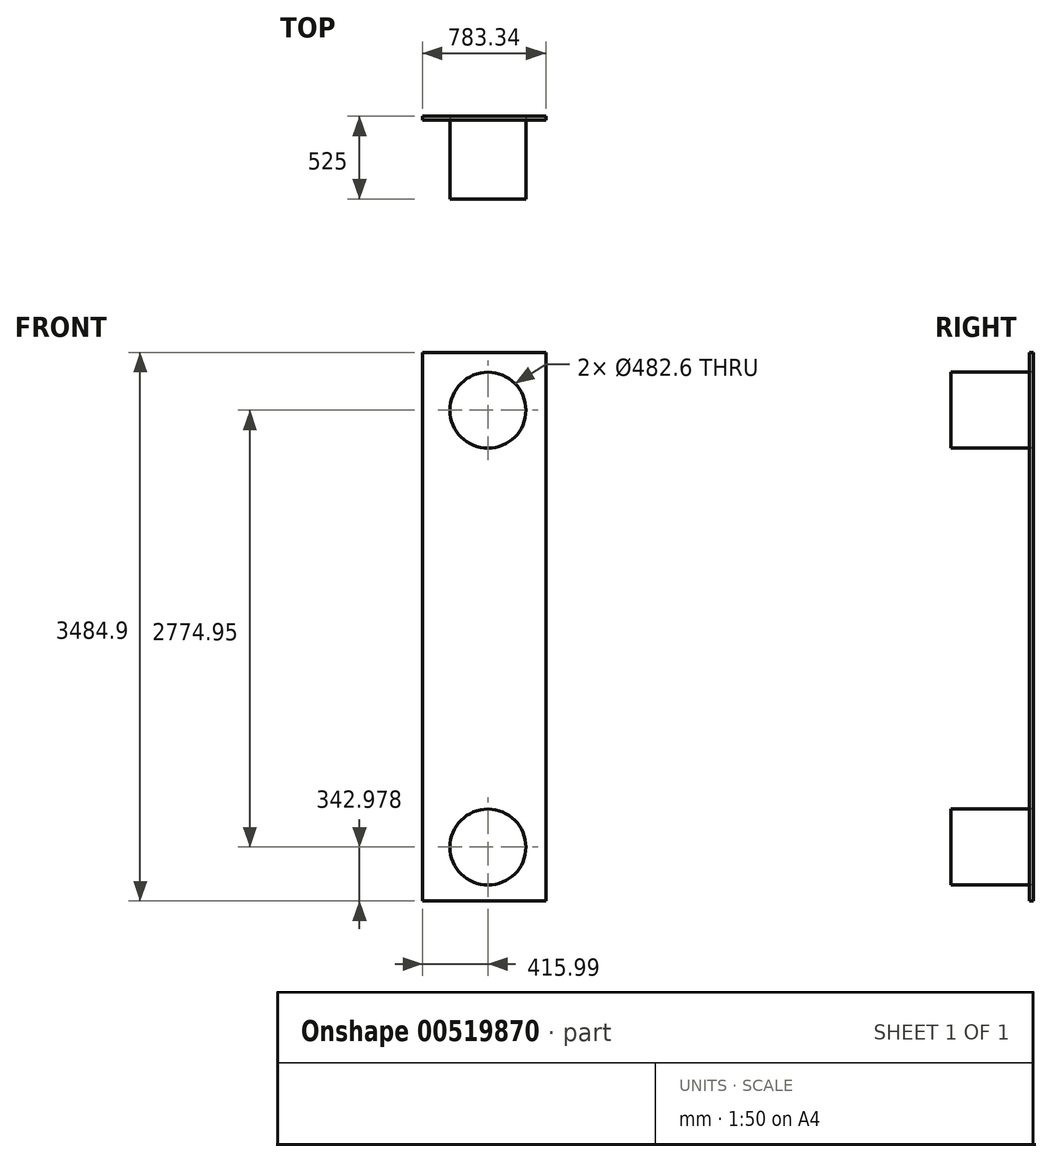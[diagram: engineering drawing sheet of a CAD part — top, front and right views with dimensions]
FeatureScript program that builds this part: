
annotation { "Feature Type Name" : "Feature", "Feature Type Description" : "" }
export const myFeature = defineFeature(function(context is Context, id is Id, definition is map)
    precondition{}
    {
        {
            var Q0;
            Q0=qCreatedBy(makeId("Front.planeOp"),FACE);
            var sketch = newSketch(context, id + "F0", { "sketchPlane" : qUnion([Q0])});
            skCircle(sketch, "E0", {"center": v(0, -900.07) * mm, "radius": 241.3 * mm});
            skCircle(sketch, "E1", {"center": v(0, 1874.88) * mm, "radius": 241.3 * mm});
            skLineSegment(sketch, "E2", {"start": v(0, 1874.88) * mm, "end": v(0, -900.07) * mm, "construction": true});
            skLineSegment(sketch, "E3.bottom", {"start": v(-416, 2241.85) * mm, "end": v(367.35, 2241.85) * mm});
            skLineSegment(sketch, "E3.top", {"start": v(-416, -1243.05) * mm, "end": v(367.35, -1243.05) * mm});
            skLineSegment(sketch, "E3.left", {"start": v(-416, 2241.85) * mm, "end": v(-416, -1243.05) * mm});
            skLineSegment(sketch, "E3.right", {"start": v(367.35, 2241.85) * mm, "end": v(367.35, -1243.05) * mm});
            skSolve(sketch);
        }
        {
            var Q0;
            Q0=makeQuery(id+"F0.imprint","IMPRINT",FACE,{"disambiguationData":[TD([[makeQuery(id+"F0.imprint","IMPRINT",EDGE,{"derivedFrom":sQuery(id+"F0.wireOp",EDGE,"E0")}),-1.0]])]});
            extrude(context, id + "F1", {"entities" : qUnion([Q0]), "oppositeDirection" : true, "depth" : 25 * mm, "offsetDistance" : 25 * mm});
        }
        {
            var Q0;
            Q0=makeQuery(id+"F0.imprint","IMPRINT",FACE,{"disambiguationData":[TD([[makeQuery(id+"F0.imprint","IMPRINT",EDGE,{"derivedFrom":sQuery(id+"F0.wireOp",EDGE,"E1")}),1.0]])]});
            var Q1;
            Q1=makeQuery(id+"F0.imprint","IMPRINT",FACE,{"disambiguationData":[TD([[makeQuery(id+"F0.imprint","IMPRINT",EDGE,{"derivedFrom":sQuery(id+"F0.wireOp",EDGE,"E0")}),1.0]])]});
            extrude(context, id + "F2", {"entities" : qUnion([Q0, Q1]), "depth" : 500 * mm, "offsetDistance" : 25 * mm});
        }
    });
